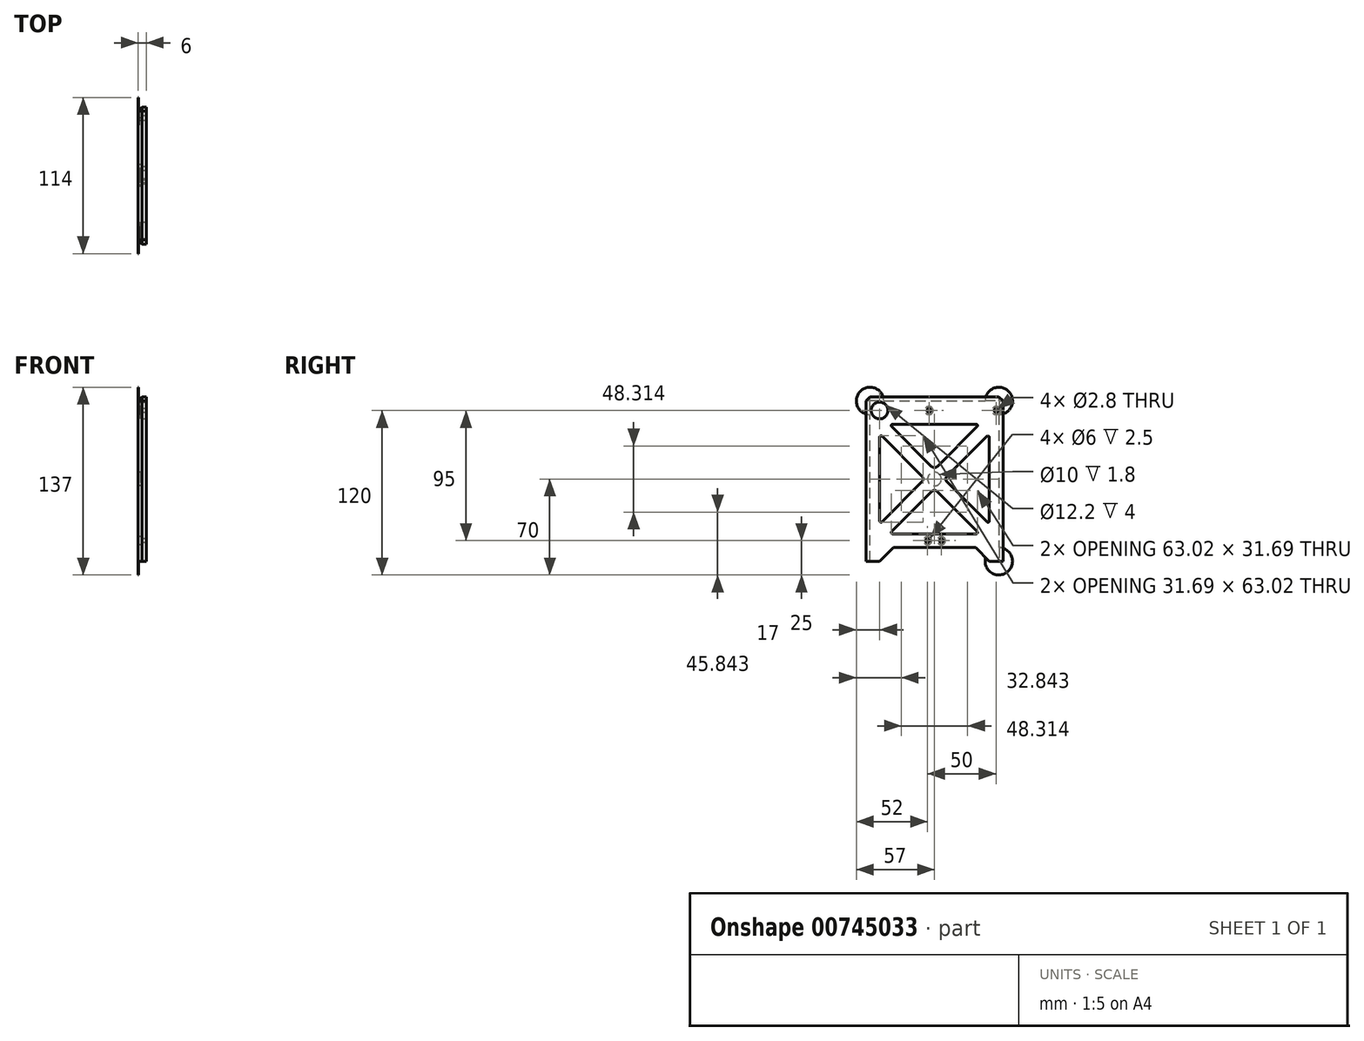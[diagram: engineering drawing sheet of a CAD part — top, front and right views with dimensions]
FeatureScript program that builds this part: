
annotation { "Feature Type Name" : "Feature", "Feature Type Description" : "" }
export const myFeature = defineFeature(function(context is Context, id is Id, definition is map)
    precondition{}
    {
        {
            var Q0;
            Q0=qCreatedBy(makeId("Right.planeOp"),FACE);
            var sketch = newSketch(context, id + "F0", { "sketchPlane" : qUnion([Q0])});
            skLineSegment(sketch, "E0.bottom", {"start": v(50, -60) * mm, "end": v(40.05, -60) * mm});
            skLineSegment(sketch, "E0.top", {"start": v(50, 60) * mm, "end": v(-50, 60) * mm});
            skLineSegment(sketch, "E0.left", {"start": v(50, -60) * mm, "end": v(50, 60) * mm});
            skLineSegment(sketch, "E0.right", {"start": v(-50, -60) * mm, "end": v(-50, 60) * mm});
            skPoint(sketch, "E0.middle", {"position": v(0, 0) * mm});
            skLineSegment(sketch, "E1.bottom", {"start": v(40, -40) * mm, "end": v(-32.93, -40) * mm});
            skLineSegment(sketch, "E1.top", {"start": v(32.93, 40) * mm, "end": v(-32.93, 40) * mm});
            skLineSegment(sketch, "E1.left", {"start": v(40, -40) * mm, "end": v(40, 32.93) * mm});
            skLineSegment(sketch, "E1.right", {"start": v(-40, -32.93) * mm, "end": v(-40, 32.93) * mm});
            skLineSegment(sketch, "E2.trimOffspring", {"start": v(-40, -60) * mm, "end": v(-50, -60) * mm});
            skLineSegment(sketch, "E3", {"start": v(30.05, -50) * mm, "end": v(40.05, -60) * mm});
            skLineSegment(sketch, "E4", {"start": v(30.05, -50) * mm, "end": v(-29.95, -50) * mm});
            skLineSegment(sketch, "E5", {"start": v(-29.95, -50) * mm, "end": v(-40, -60) * mm});
            skLineSegment(sketch, "E6", {"start": v(-40, -32.93) * mm, "end": v(-9.2, -2.12) * mm});
            skLineSegment(sketch, "E7.MirrorCS", {"start": v(-32.93, -40) * mm, "end": v(-2.12, -9.2) * mm});
            skLineSegment(sketch, "E8.trimOffspring", {"start": v(-40, 32.93) * mm, "end": v(-9.2, 2.12) * mm});
            skLineSegment(sketch, "E9.MirrorCS", {"start": v(-32.93, 40) * mm, "end": v(-2.12, 9.2) * mm});
            skLineSegment(sketch, "E10.trimOffspring", {"start": v(9.2, 2.12) * mm, "end": v(40, 32.93) * mm});
            skLineSegment(sketch, "E11.trimOffspring", {"start": v(2.12, -9.2) * mm, "end": v(32.93, -40) * mm});
            skLineSegment(sketch, "E12.trimOffspring", {"start": v(9.2, -2.12) * mm, "end": v(40, -32.93) * mm});
            skLineSegment(sketch, "E13.trimOffspring", {"start": v(2.12, 9.2) * mm, "end": v(32.93, 40) * mm});
            skPoint(sketch, "E14.visualSharp", {"position": v(0, 7.07) * mm});
            skArc(sketch, "E14.filletArc", {"start": v(-2.12, 9.2) * mm, "mid": v(0, 8.31) * mm, "end": v(2.12, 9.2) * mm});
            skPoint(sketch, "E15.visualSharp", {"position": v(0, -7.07) * mm});
            skArc(sketch, "E15.filletArc", {"start": v(2.12, -9.2) * mm, "mid": v(0, -8.31) * mm, "end": v(-2.12, -9.2) * mm});
            skPoint(sketch, "E16.visualSharp", {"position": v(7.07, 0) * mm});
            skArc(sketch, "E16.filletArc", {"start": v(9.2, 2.12) * mm, "mid": v(8.31, 0) * mm, "end": v(9.2, -2.12) * mm});
            skPoint(sketch, "E17.visualSharp", {"position": v(-7.07, 0) * mm});
            skArc(sketch, "E17.filletArc", {"start": v(-9.2, -2.12) * mm, "mid": v(-8.31, 0) * mm, "end": v(-9.2, 2.12) * mm});
            skLineSegment(sketch, "E18", {"start": v(81.83, 50) * mm, "end": v(-92.03, 50) * mm, "construction": true});
            skPoint(sketch, "E19", {"position": v(45, 50) * mm});
            skPoint(sketch, "E20", {"position": v(-4, 50) * mm});
            skSolve(sketch);
        }
        {
            var Q0;
            Q0=qSketchRegion(id+"F0",true);
            extrude(context, id + "F1", {"entities" : qUnion([Q0]), "depth" : 6 * mm, "offsetDistance" : 25 * mm});
        }
        {
            var Q0;
            Q0=makeQuery(id+"F1.opExtrude","SWEPT_EDGE",EDGE,{"disambiguationData":[OSD([sQuery(id+"F0.wireOp",EDGE,"E1.top"),sQuery(id+"F0.wireOp",EDGE,"E9.MirrorCS")])]});
            var Q1;
            Q1=makeQuery(id+"F1.opExtrude","SWEPT_EDGE",EDGE,{"disambiguationData":[OSD([sQuery(id+"F0.wireOp",EDGE,"E1.top"),sQuery(id+"F0.wireOp",EDGE,"E13.trimOffspring")])]});
            var Q2;
            Q2=makeQuery(id+"F1.opExtrude","SWEPT_EDGE",EDGE,{"disambiguationData":[OSD([sQuery(id+"F0.wireOp",EDGE,"E1.right"),sQuery(id+"F0.wireOp",EDGE,"E8.trimOffspring")])]});
            var Q3;
            Q3=makeQuery(id+"F1.opExtrude","SWEPT_EDGE",EDGE,{"disambiguationData":[OSD([sQuery(id+"F0.wireOp",EDGE,"E1.right"),sQuery(id+"F0.wireOp",EDGE,"E6")])]});
            var Q4;
            Q4=makeQuery(id+"F1.opExtrude","SWEPT_EDGE",EDGE,{"disambiguationData":[OSD([sQuery(id+"F0.wireOp",EDGE,"E1.bottom"),sQuery(id+"F0.wireOp",EDGE,"E7.MirrorCS")])]});
            var Q5;
            Q5=makeQuery(id+"F1.opExtrude","SWEPT_EDGE",EDGE,{"disambiguationData":[OSD([sQuery(id+"F0.wireOp",EDGE,"E1.left"),sQuery(id+"F0.wireOp",EDGE,"E10.trimOffspring")])]});
            var Q6;
            Q6=makeQuery(id+"F1.opExtrude","SWEPT_EDGE",EDGE,{"disambiguationData":[OSD([sQuery(id+"F0.wireOp",EDGE,"E1.left"),sQuery(id+"F0.wireOp",EDGE,"E12.trimOffspring")])]});
            var Q7;
            Q7=makeQuery(id+"F1.opExtrude","SWEPT_EDGE",EDGE,{"disambiguationData":[OSD([sQuery(id+"F0.wireOp",EDGE,"E1.bottom"),sQuery(id+"F0.wireOp",EDGE,"E11.trimOffspring")])]});
            fillet(context, id + "F2", {"entities" : qUnion([Q0, Q1, Q2, Q3, Q4, Q5, Q6, Q7]), "radius" : 1 * mm, "tangentPropagation" : true, "allowEdgeOverflow" : false});
        }
        {
            var Q0;
            Q0=makeQuery(id+"F1.opExtrude","CAP_FACE",FACE,{"disambiguationData":[OSD([sQuery(id+"F0.wireOp",EDGE,"E0.bottom"),sQuery(id+"F0.wireOp",EDGE,"E0.top"),sQuery(id+"F0.wireOp",EDGE,"E0.left"),sQuery(id+"F0.wireOp",EDGE,"E0.right"),sQuery(id+"F0.wireOp",EDGE,"E1.bottom"),sQuery(id+"F0.wireOp",EDGE,"E1.top"),sQuery(id+"F0.wireOp",EDGE,"E1.left"),sQuery(id+"F0.wireOp",EDGE,"E1.right"),sQuery(id+"F0.wireOp",EDGE,"E2.trimOffspring"),sQuery(id+"F0.wireOp",EDGE,"E3"),sQuery(id+"F0.wireOp",EDGE,"E4"),sQuery(id+"F0.wireOp",EDGE,"E5"),sQuery(id+"F0.wireOp",EDGE,"E6"),sQuery(id+"F0.wireOp",EDGE,"E7.MirrorCS"),sQuery(id+"F0.wireOp",EDGE,"E8.trimOffspring"),sQuery(id+"F0.wireOp",EDGE,"E9.MirrorCS"),sQuery(id+"F0.wireOp",EDGE,"E10.trimOffspring"),sQuery(id+"F0.wireOp",EDGE,"E11.trimOffspring"),sQuery(id+"F0.wireOp",EDGE,"E12.trimOffspring"),sQuery(id+"F0.wireOp",EDGE,"E13.trimOffspring"),sQuery(id+"F0.wireOp",EDGE,"E14.filletArc"),sQuery(id+"F0.wireOp",EDGE,"E15.filletArc"),sQuery(id+"F0.wireOp",EDGE,"E16.filletArc"),sQuery(id+"F0.wireOp",EDGE,"E17.filletArc")])],"isStart":true});
            var sketch = newSketch(context, id + "F3", { "sketchPlane" : qUnion([Q0])});
            skCircle(sketch, "E21", {"center": v(0, 0) * mm, "radius": 5 * mm});
            skSolve(sketch);
        }
        {
            var Q0;
            Q0=makeQuery(id+"F3.imprint","IMPRINT",FACE,{"disambiguationData":[TD([[makeQuery(id+"F3.imprint","IMPRINT",EDGE,{"derivedFrom":sQuery(id+"F3.wireOp",EDGE,"E21")}),1.0]])]});
            extrude(context, id + "F4", {"entities" : qUnion([Q0]), "operationType" : NewBodyOperationType.REMOVE, "oppositeDirection" : true, "depth" : 1.8 * mm, "offsetDistance" : 25 * mm});
        }
        {
            var Q0;
            {var subQ0=sQuery(id+"F0.wireOp",EDGE,"E0.left");var subQ1=sQuery(id+"F0.wireOp",EDGE,"E0.top");var subQ2=sQuery(id+"F0.wireOp",EDGE,"E0.right");var subQ3=sQuery(id+"F0.wireOp",EDGE,"E2.trimOffspring");var subQ4=sQuery(id+"F0.wireOp",EDGE,"E0.bottom");Q0=makeQuery(id+"F9.boolean.opBoolean","MERGE",FACE,{"derivedFrom":[makeQuery(id+"F1.opExtrude","CAP_FACE",FACE,{"disambiguationData":[OSD([subQ4,subQ1,subQ0,subQ2,sQuery(id+"F0.wireOp",EDGE,"E1.bottom"),sQuery(id+"F0.wireOp",EDGE,"E1.top"),sQuery(id+"F0.wireOp",EDGE,"E1.left"),sQuery(id+"F0.wireOp",EDGE,"E1.right"),subQ3,sQuery(id+"F0.wireOp",EDGE,"E3"),sQuery(id+"F0.wireOp",EDGE,"E4"),sQuery(id+"F0.wireOp",EDGE,"E5"),sQuery(id+"F0.wireOp",EDGE,"E6"),sQuery(id+"F0.wireOp",EDGE,"E7.MirrorCS"),sQuery(id+"F0.wireOp",EDGE,"E8.trimOffspring"),sQuery(id+"F0.wireOp",EDGE,"E9.MirrorCS"),sQuery(id+"F0.wireOp",EDGE,"E10.trimOffspring"),sQuery(id+"F0.wireOp",EDGE,"E11.trimOffspring"),sQuery(id+"F0.wireOp",EDGE,"E12.trimOffspring"),sQuery(id+"F0.wireOp",EDGE,"E13.trimOffspring"),sQuery(id+"F0.wireOp",EDGE,"E14.filletArc"),sQuery(id+"F0.wireOp",EDGE,"E15.filletArc"),sQuery(id+"F0.wireOp",EDGE,"E16.filletArc"),sQuery(id+"F0.wireOp",EDGE,"E17.filletArc")])],"isStart":true}),makeQuery(id+"F9.opExtrude","CAP_FACE",FACE,{"disambiguationData":[OSD([subQ4,subQ0,sQuery(id+"F8.wireOp",EDGE,"PSrgGkol-MO8q-g1fu-dDRE-y41ujJaxh7FT")])],"isStart":true}),makeQuery(id+"F9.opExtrude","CAP_FACE",FACE,{"disambiguationData":[OSD([subQ2,subQ3,sQuery(id+"F8.wireOp",EDGE,"1aKPLW1Y-IE5d-4tmK-5bFR-xkpx61fHem11")])],"isStart":true}),makeQuery(id+"F9.opExtrude","CAP_FACE",FACE,{"disambiguationData":[OSD([subQ1,subQ2,sQuery(id+"F8.wireOp",EDGE,"02GekRd3-WHB3-A6C6-mmOw-hFaiTY61e2sP")])],"isStart":true}),makeQuery(id+"F9.opExtrude","CAP_FACE",FACE,{"disambiguationData":[OSD([subQ1,subQ0,sQuery(id+"F8.wireOp",EDGE,"ECdukxah-RqsZ-JlNO-yzCW-vx4sxx8bxQE0")])],"isStart":true})]});}
            var sketch = newSketch(context, id + "F5", { "sketchPlane" : qUnion([Q0])});
            skPoint(sketch, "E22", {"position": v(-5, -45) * mm});
            skPoint(sketch, "E23.MirrorP", {"position": v(5, -45) * mm});
            skSolve(sketch);
        }
        {
            var Q0;
            Q0=sQuery(id+"F5.wireOp",VERTEX,"E22");
            var Q1;
            Q1=sQuery(id+"F5.wireOp",VERTEX,"E23.MirrorP");
            var Q2;
            Q2=makeQuery(id+"F1.opExtrude","SWEPT_BODY",BODY,{"disambiguationData":[OSD([sQuery(id+"F0.wireOp",EDGE,"E0.bottom"),sQuery(id+"F0.wireOp",EDGE,"E0.top"),sQuery(id+"F0.wireOp",EDGE,"E0.left"),sQuery(id+"F0.wireOp",EDGE,"E0.right"),sQuery(id+"F0.wireOp",EDGE,"E1.bottom"),sQuery(id+"F0.wireOp",EDGE,"E1.top"),sQuery(id+"F0.wireOp",EDGE,"E1.left"),sQuery(id+"F0.wireOp",EDGE,"E1.right"),sQuery(id+"F0.wireOp",EDGE,"E2.trimOffspring"),sQuery(id+"F0.wireOp",EDGE,"E3"),sQuery(id+"F0.wireOp",EDGE,"E4"),sQuery(id+"F0.wireOp",EDGE,"E5"),sQuery(id+"F0.wireOp",EDGE,"E6"),sQuery(id+"F0.wireOp",EDGE,"E7.MirrorCS"),sQuery(id+"F0.wireOp",EDGE,"E8.trimOffspring"),sQuery(id+"F0.wireOp",EDGE,"E9.MirrorCS"),sQuery(id+"F0.wireOp",EDGE,"E10.trimOffspring"),sQuery(id+"F0.wireOp",EDGE,"E11.trimOffspring"),sQuery(id+"F0.wireOp",EDGE,"E12.trimOffspring"),sQuery(id+"F0.wireOp",EDGE,"E13.trimOffspring"),sQuery(id+"F0.wireOp",EDGE,"E14.filletArc"),sQuery(id+"F0.wireOp",EDGE,"E15.filletArc"),sQuery(id+"F0.wireOp",EDGE,"E16.filletArc"),sQuery(id+"F0.wireOp",EDGE,"E17.filletArc")])]});
            hole(context, id + "F6", {"style" : HoleStyle.C_BORE, "endStyle" : HoleEndStyle.THROUGH, "holeDiameter" : 2.8 * mm, "cBoreDiameter" : 6 * mm, "cBoreDepth" : 2.5 * mm, "majorDiameter" : 5 * mm, "isTappedThrough" : true, "tappedDepth" : 6 * mm, "tapClearance" : 3, "locations" : qUnion([Q0, Q1]), "scope" : qUnion([Q2])});
        }
        {
            var Q0;
            Q0=makeQuery(id+"F1.opExtrude","SWEPT_EDGE",EDGE,{"disambiguationData":[OSD([sQuery(id+"F0.wireOp",EDGE,"E0.top"),sQuery(id+"F0.wireOp",EDGE,"E0.right")])]});
            var Q1;
            Q1=makeQuery(id+"F1.opExtrude","SWEPT_EDGE",EDGE,{"disambiguationData":[OSD([sQuery(id+"F0.wireOp",EDGE,"E0.top"),sQuery(id+"F0.wireOp",EDGE,"E0.left")])]});
            var Q2;
            Q2=makeQuery(id+"F1.opExtrude","CAP_EDGE",EDGE,{"disambiguationData":[OSD([sQuery(id+"F0.wireOp",EDGE,"E0.right")])],"isStart":true});
            var Q3;
            Q3=makeQuery(id+"F1.opExtrude","CAP_EDGE",EDGE,{"disambiguationData":[OSD([sQuery(id+"F0.wireOp",EDGE,"E0.left")])],"isStart":true});
            var Q4;
            Q4=makeQuery(id+"F1.opExtrude","CAP_EDGE",EDGE,{"disambiguationData":[OSD([sQuery(id+"F0.wireOp",EDGE,"E0.top")])],"isStart":true});
            chamfer(context, id + "F7", {"entities" : qUnion([Q0, Q1, Q2, Q3, Q4]), "width" : 3 * mm, "tangentPropagation" : true});
        }
        {
            var Q0;
            Q0=makeQuery(id+"F1.opExtrude","CAP_FACE",FACE,{"disambiguationData":[OSD([sQuery(id+"F0.wireOp",EDGE,"E0.bottom"),sQuery(id+"F0.wireOp",EDGE,"E0.top"),sQuery(id+"F0.wireOp",EDGE,"E0.left"),sQuery(id+"F0.wireOp",EDGE,"E0.right"),sQuery(id+"F0.wireOp",EDGE,"E1.bottom"),sQuery(id+"F0.wireOp",EDGE,"E1.top"),sQuery(id+"F0.wireOp",EDGE,"E1.left"),sQuery(id+"F0.wireOp",EDGE,"E1.right"),sQuery(id+"F0.wireOp",EDGE,"E2.trimOffspring"),sQuery(id+"F0.wireOp",EDGE,"E3"),sQuery(id+"F0.wireOp",EDGE,"E4"),sQuery(id+"F0.wireOp",EDGE,"E5"),sQuery(id+"F0.wireOp",EDGE,"E6"),sQuery(id+"F0.wireOp",EDGE,"E7.MirrorCS"),sQuery(id+"F0.wireOp",EDGE,"E8.trimOffspring"),sQuery(id+"F0.wireOp",EDGE,"E9.MirrorCS"),sQuery(id+"F0.wireOp",EDGE,"E10.trimOffspring"),sQuery(id+"F0.wireOp",EDGE,"E11.trimOffspring"),sQuery(id+"F0.wireOp",EDGE,"E12.trimOffspring"),sQuery(id+"F0.wireOp",EDGE,"E13.trimOffspring"),sQuery(id+"F0.wireOp",EDGE,"E14.filletArc"),sQuery(id+"F0.wireOp",EDGE,"E15.filletArc"),sQuery(id+"F0.wireOp",EDGE,"E16.filletArc"),sQuery(id+"F0.wireOp",EDGE,"E17.filletArc")])],"isStart":true});
            var sketch = newSketch(context, id + "F8", { "sketchPlane" : qUnion([Q0])});
            skPoint(sketch, "E24", {"position": v(-47, 57) * mm});
            skPoint(sketch, "E25", {"position": v(47, 57) * mm});
            skPoint(sketch, "E26", {"position": v(47, -60) * mm});
            skPoint(sketch, "E27", {"position": v(-47, -60) * mm});
            skArc(sketch, "E28", {"start": v(-37, 57) * mm, "mid": v(-54.07, 64.07) * mm, "end": v(-47, 47) * mm});
            skArc(sketch, "E29", {"start": v(47, 47) * mm, "mid": v(54.07, 64.07) * mm, "end": v(37, 57) * mm});
            skArc(sketch, "E30", {"start": v(47, -50) * mm, "mid": v(53.07, -67.95) * mm, "end": v(37.35, -57.37) * mm});
            skArc(sketch, "E31", {"start": v(-47, -50) * mm, "mid": v(-53.05, -67.96) * mm, "end": v(-37.37, -57.32) * mm});
            skSolve(sketch);
        }
        {
            var Q0;
            {var subQ0=sQuery(id+"F8.wireOp",EDGE,"E28");Q0=makeQuery(id+"F8.imprint","IMPRINT",FACE,{"disambiguationData":[TD([[makeQuery(id+"F8.imprint","IMPRINT",EDGE,{"derivedFrom":subQ0}),1.0]])]});}
            var Q1;
            {var subQ0=sQuery(id+"F8.wireOp",EDGE,"E29");Q1=makeQuery(id+"F8.imprint","IMPRINT",FACE,{"disambiguationData":[TD([[makeQuery(id+"F8.imprint","IMPRINT",EDGE,{"derivedFrom":subQ0}),1.0]])]});}
            var Q2;
            {var subQ0=sQuery(id+"F8.wireOp",EDGE,"E31");Q2=makeQuery(id+"F8.imprint","IMPRINT",FACE,{"disambiguationData":[TD([[makeQuery(id+"F8.imprint","IMPRINT",EDGE,{"derivedFrom":subQ0}),1.0]])]});}
            var Q3;
            {var subQ0=sQuery(id+"F8.wireOp",EDGE,"E30");Q3=makeQuery(id+"F8.imprint","IMPRINT",FACE,{"disambiguationData":[TD([[makeQuery(id+"F8.imprint","IMPRINT",EDGE,{"derivedFrom":subQ0}),-1.0]])]});}
            extrude(context, id + "F9", {"entities" : qUnion([Q0, Q1, Q2, Q3]), "operationType" : NewBodyOperationType.ADD, "oppositeDirection" : true, "depth" : 0.4 * mm, "offsetDistance" : 25 * mm});
        }
        {
            var Q0;
            Q0=sQuery(id+"F0.wireOp",VERTEX,"E20");
            var Q1;
            Q1=sQuery(id+"F0.wireOp",VERTEX,"E19");
            var Q2;
            Q2=makeQuery(id+"F1.opExtrude","SWEPT_BODY",BODY,{"disambiguationData":[OSD([sQuery(id+"F0.wireOp",EDGE,"E0.bottom"),sQuery(id+"F0.wireOp",EDGE,"E0.top"),sQuery(id+"F0.wireOp",EDGE,"E0.left"),sQuery(id+"F0.wireOp",EDGE,"E0.right"),sQuery(id+"F0.wireOp",EDGE,"E1.bottom"),sQuery(id+"F0.wireOp",EDGE,"E1.top"),sQuery(id+"F0.wireOp",EDGE,"E1.left"),sQuery(id+"F0.wireOp",EDGE,"E1.right"),sQuery(id+"F0.wireOp",EDGE,"E2.trimOffspring"),sQuery(id+"F0.wireOp",EDGE,"E3"),sQuery(id+"F0.wireOp",EDGE,"E4"),sQuery(id+"F0.wireOp",EDGE,"E5"),sQuery(id+"F0.wireOp",EDGE,"E6"),sQuery(id+"F0.wireOp",EDGE,"E7.MirrorCS"),sQuery(id+"F0.wireOp",EDGE,"E8.trimOffspring"),sQuery(id+"F0.wireOp",EDGE,"E9.MirrorCS"),sQuery(id+"F0.wireOp",EDGE,"E10.trimOffspring"),sQuery(id+"F0.wireOp",EDGE,"E11.trimOffspring"),sQuery(id+"F0.wireOp",EDGE,"E12.trimOffspring"),sQuery(id+"F0.wireOp",EDGE,"E13.trimOffspring"),sQuery(id+"F0.wireOp",EDGE,"E14.filletArc"),sQuery(id+"F0.wireOp",EDGE,"E15.filletArc"),sQuery(id+"F0.wireOp",EDGE,"E16.filletArc"),sQuery(id+"F0.wireOp",EDGE,"E17.filletArc")])]});
            hole(context, id + "F10", {"style" : HoleStyle.C_BORE, "endStyle" : HoleEndStyle.THROUGH, "oppositeDirection" : true, "holeDiameter" : 2.8 * mm, "cBoreDiameter" : 6 * mm, "cBoreDepth" : 2.5 * mm, "majorDiameter" : 5 * mm, "isTappedThrough" : true, "tappedDepth" : 6 * mm, "tapClearance" : 3, "locations" : qUnion([Q0, Q1]), "scope" : qUnion([Q2])});
        }
        {
            var Q0;
            Q0=makeQuery(id+"F1.opExtrude","CAP_FACE",FACE,{"disambiguationData":[OSD([sQuery(id+"F0.wireOp",EDGE,"E0.bottom"),sQuery(id+"F0.wireOp",EDGE,"E0.top"),sQuery(id+"F0.wireOp",EDGE,"E0.left"),sQuery(id+"F0.wireOp",EDGE,"E0.right"),sQuery(id+"F0.wireOp",EDGE,"E1.bottom"),sQuery(id+"F0.wireOp",EDGE,"E1.top"),sQuery(id+"F0.wireOp",EDGE,"E1.left"),sQuery(id+"F0.wireOp",EDGE,"E1.right"),sQuery(id+"F0.wireOp",EDGE,"E2.trimOffspring"),sQuery(id+"F0.wireOp",EDGE,"E3"),sQuery(id+"F0.wireOp",EDGE,"E4"),sQuery(id+"F0.wireOp",EDGE,"E5"),sQuery(id+"F0.wireOp",EDGE,"E6"),sQuery(id+"F0.wireOp",EDGE,"E7.MirrorCS"),sQuery(id+"F0.wireOp",EDGE,"E8.trimOffspring"),sQuery(id+"F0.wireOp",EDGE,"E9.MirrorCS"),sQuery(id+"F0.wireOp",EDGE,"E10.trimOffspring"),sQuery(id+"F0.wireOp",EDGE,"E11.trimOffspring"),sQuery(id+"F0.wireOp",EDGE,"E12.trimOffspring"),sQuery(id+"F0.wireOp",EDGE,"E13.trimOffspring"),sQuery(id+"F0.wireOp",EDGE,"E14.filletArc"),sQuery(id+"F0.wireOp",EDGE,"E15.filletArc"),sQuery(id+"F0.wireOp",EDGE,"E16.filletArc"),sQuery(id+"F0.wireOp",EDGE,"E17.filletArc")])],"isStart":false});
            var sketch = newSketch(context, id + "F11", { "sketchPlane" : qUnion([Q0])});
            skCircle(sketch, "E32", {"center": v(-40, 50) * mm, "radius": 6.1 * mm});
            skSolve(sketch);
        }
        {
            var Q0;
            Q0=makeQuery(id+"F11.imprint","IMPRINT",FACE,{"disambiguationData":[TD([[makeQuery(id+"F11.imprint","IMPRINT",EDGE,{"derivedFrom":sQuery(id+"F11.wireOp",EDGE,"E32")}),1.0]])]});
            extrude(context, id + "F12", {"entities" : qUnion([Q0]), "operationType" : NewBodyOperationType.REMOVE, "oppositeDirection" : true, "depth" : 4 * mm, "offsetDistance" : 25 * mm});
        }
        {
            var Q0;
            Q0=makeQuery(id+"F9.opExtrude","CAP_FACE",FACE,{"disambiguationData":[OSD([sQuery(id+"F0.wireOp",EDGE,"E0.bottom"),sQuery(id+"F0.wireOp",EDGE,"E0.top"),sQuery(id+"F0.wireOp",EDGE,"E0.left"),sQuery(id+"F0.wireOp",EDGE,"E0.right"),sQuery(id+"F0.wireOp",EDGE,"E1.bottom"),sQuery(id+"F0.wireOp",EDGE,"E1.top"),sQuery(id+"F0.wireOp",EDGE,"E1.left"),sQuery(id+"F0.wireOp",EDGE,"E1.right"),sQuery(id+"F0.wireOp",EDGE,"E2.trimOffspring"),sQuery(id+"F0.wireOp",EDGE,"E3"),sQuery(id+"F0.wireOp",EDGE,"E4"),sQuery(id+"F0.wireOp",EDGE,"E5"),sQuery(id+"F0.wireOp",EDGE,"E6"),sQuery(id+"F0.wireOp",EDGE,"E7.MirrorCS"),sQuery(id+"F0.wireOp",EDGE,"E8.trimOffspring"),sQuery(id+"F0.wireOp",EDGE,"E9.MirrorCS"),sQuery(id+"F0.wireOp",EDGE,"E10.trimOffspring"),sQuery(id+"F0.wireOp",EDGE,"E11.trimOffspring"),sQuery(id+"F0.wireOp",EDGE,"E12.trimOffspring"),sQuery(id+"F0.wireOp",EDGE,"E13.trimOffspring"),sQuery(id+"F0.wireOp",EDGE,"E14.filletArc"),sQuery(id+"F0.wireOp",EDGE,"E15.filletArc"),sQuery(id+"F0.wireOp",EDGE,"E16.filletArc"),sQuery(id+"F0.wireOp",EDGE,"E17.filletArc"),sQuery(id+"F8.wireOp",EDGE,"E28")])],"isStart":false});
            var sketch = newSketch(context, id + "F13", { "sketchPlane" : qUnion([Q0])});
            skLineSegment(sketch, "E33", {"start": v(47.4, 47) * mm, "end": v(47.4, 53) * mm});
            skLineSegment(sketch, "E34", {"start": v(47.4, 47) * mm, "end": v(48.31, 48.2) * mm});
            skLineSegment(sketch, "E35", {"start": v(48.31, 48.2) * mm, "end": v(48.31, 51.8) * mm});
            skLineSegment(sketch, "E36", {"start": v(48.31, 51.8) * mm, "end": v(47.4, 53) * mm});
            skSolve(sketch);
        }
        {
            var Q0;
            {var subQ0=sQuery(id+"F13.wireOp",EDGE,"E34");Q0=makeQuery(id+"F13.imprint","IMPRINT",FACE,{"disambiguationData":[TD([[makeQuery(id+"F13.imprint","IMPRINT",EDGE,{"derivedFrom":subQ0}),1.0]])]});}
            extrude(context, id + "F14", {"entities" : qUnion([Q0]), "operationType" : NewBodyOperationType.ADD, "depth" : 1 * mm, "offsetDistance" : 25 * mm});
        }
    });
